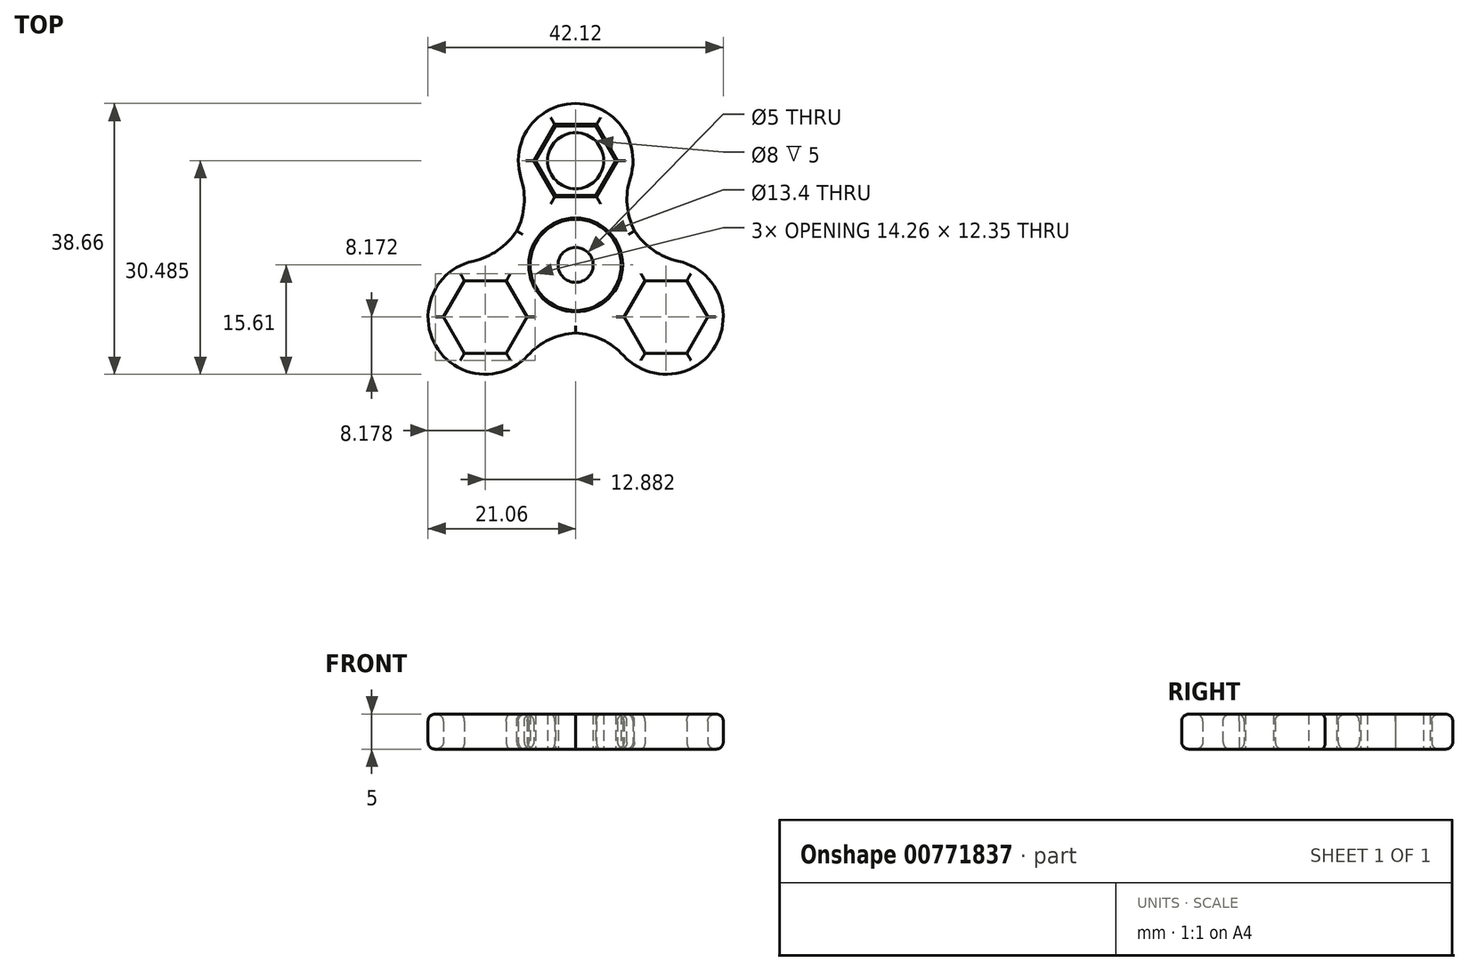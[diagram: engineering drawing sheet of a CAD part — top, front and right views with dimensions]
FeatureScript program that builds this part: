
annotation { "Feature Type Name" : "Feature", "Feature Type Description" : "" }
export const myFeature = defineFeature(function(context is Context, id is Id, definition is map)
    precondition{}
    {
        {
            assignVariable(context, id + "F0", {"name" : "Extrude", "anyValue" : 5});
        }
        {
            assignVariable(context, id + "F1", {"name" : "Brate", "anyValue" : 3});
        }
        {
            var Q0;
            Q0=qCreatedBy(makeId("Top.planeOp"),FACE);
            var sketch = newSketch(context, id + "F2", { "sketchPlane" : qUnion([Q0])});
            skCircle(sketch, "E0", {"center": v(0, 0) * mm, "radius": 2.5 * mm});
            skCircle(sketch, "E1", {"center": v(0, 0) * mm, "radius": 6.5 * mm});
            skCircle(sketch, "E2.0", {"center": v(0, 0) * mm, "radius": 6.7 * mm});
            skCircle(sketch, "E3.0", {"center": v(0, 0) * mm, "radius": 9.7 * mm});
            skCircle(sketch, "E4.cCircle", {"center": v(0, 14.88) * mm, "radius": 4.95 * mm, "construction": true});
            skLineSegment(sketch, "E4.0", {"start": v(5.72, 14.88) * mm, "end": v(2.86, 9.92) * mm});
            skLineSegment(sketch, "E4.1", {"start": v(2.86, 9.92) * mm, "end": v(-2.86, 9.92) * mm});
            skLineSegment(sketch, "E4.2", {"start": v(-2.86, 9.92) * mm, "end": v(-5.72, 14.88) * mm});
            skLineSegment(sketch, "E4.3", {"start": v(-5.72, 14.88) * mm, "end": v(-2.86, 19.83) * mm});
            skLineSegment(sketch, "E4.4", {"start": v(-2.86, 19.83) * mm, "end": v(2.86, 19.83) * mm});
            skLineSegment(sketch, "E4.5", {"start": v(2.86, 19.83) * mm, "end": v(5.72, 14.87) * mm});
            skPoint(sketch, "E4.0.midPoint", {"position": v(4.29, 12.4) * mm});
            skLineSegment(sketch, "E5.0", {"start": v(-2.99, 9.7) * mm, "end": v(-5.98, 14.88) * mm});
            skLineSegment(sketch, "E5.1", {"start": v(-2.99, 20.05) * mm, "end": v(2.99, 20.05) * mm});
            skLineSegment(sketch, "E5.2", {"start": v(2.99, 20.05) * mm, "end": v(5.98, 14.87) * mm});
            skLineSegment(sketch, "E5.3", {"start": v(-5.98, 14.88) * mm, "end": v(-2.99, 20.05) * mm});
            skLineSegment(sketch, "E5.4", {"start": v(5.98, 14.87) * mm, "end": v(2.99, 9.7) * mm});
            skLineSegment(sketch, "E5.5", {"start": v(2.99, 9.7) * mm, "end": v(-2.99, 9.7) * mm});
            skCircle(sketch, "E6.0", {"center": v(0, 14.88) * mm, "radius": 8.18 * mm});
            skCircle(sketch, "E7", {"center": v(0, 14.88) * mm, "radius": 4 * mm});
            skSolve(sketch);
        }
        {
            var Q0;
            {var subQ0=sQuery(id+"F2.wireOp",EDGE,"E5.0");Q0=makeQuery(id+"F2.imprint","IMPRINT",FACE,{"disambiguationData":[TD([[makeQuery(id+"F2.imprint","IMPRINT",EDGE,{"derivedFrom":subQ0}),1.0]])]});}
            var Q1;
            {var subQ0=sQuery(id+"F2.wireOp",EDGE,"E3.0");var subQ1=makeQuery(id+"F2.imprint","INTERSECT",VERTEX,{"derivedFrom":[subQ0,sQuery(id+"F2.wireOp",EDGE,"E5.5")]});Q1=makeQuery(id+"F2.imprint","IMPRINT",FACE,{"disambiguationData":[TD([[makeQuery(id+"F2.imprint","IMPRINT",EDGE,{"disambiguationData":[TD([[subQ1,1.0]])],"derivedFrom":subQ0}),1.0]])]});}
            var Q2;
            {var subQ0=sQuery(id+"F2.wireOp",EDGE,"E2.0");Q2=makeQuery(id+"F2.imprint","IMPRINT",FACE,{"disambiguationData":[TD([[makeQuery(id+"F2.imprint","IMPRINT",EDGE,{"derivedFrom":subQ0}),-1.0]])]});}
            extrude(context, id + "F3", {"entities" : qUnion([Q0, Q1, Q2]), "depth" : (getVariable(context, 'Extrude')) * mm, "offsetDistance" : 25 * mm});
        }
        {
            var Q0;
            {var subQ0=sQuery(id+"F2.wireOp",EDGE,"E3.0");var subQ1=sQuery(id+"F2.wireOp",EDGE,"1306070c-514a-42c6-8501-fb9c8bda2960.0");Q0=makeQuery(id+"F3.opExtrude","SWEPT_EDGE",EDGE,{"disambiguationData":[OSD([subQ1,subQ0]),TDD([makeQuery(id+"F2.imprint","INTERSECT",VERTEX,{"disambiguationData":[OD(0.0)],"derivedFrom":[subQ1,subQ0]})])]});}
            var Q1;
            {var subQ0=sQuery(id+"F2.wireOp",EDGE,"E3.0");var subQ1=sQuery(id+"F2.wireOp",EDGE,"1306070c-514a-42c6-8501-fb9c8bda2960.0");Q1=makeQuery(id+"F3.opExtrude","SWEPT_EDGE",EDGE,{"disambiguationData":[OSD([subQ1,subQ0]),TDD([makeQuery(id+"F2.imprint","INTERSECT",VERTEX,{"disambiguationData":[OD(1.0)],"derivedFrom":[subQ1,subQ0]})])]});}
            fillet(context, id + "F4", {"entities" : qUnion([Q0, Q1]), "radius" : 10 * mm, "tangentPropagation" : true, "allowEdgeOverflow" : false});
        }
        {
            var Q0;
            Q0=makeQuery(id+"F3.opExtrude","SWEPT_BODY",BODY,{"disambiguationData":[OSD([sQuery(id+"F2.wireOp",EDGE,"tQJWM1xx-dGoD-S2Vc-nebh-PP9qcAue4bdA"),sQuery(id+"F2.wireOp",EDGE,"a3c50200-fec0-4e6e-b60f-7094f83631b9.0"),sQuery(id+"F2.wireOp",EDGE,"6aacaa7e-477d-41c4-a672-bc6bc9144b92.0"),sQuery(id+"F2.wireOp",EDGE,"6aacaa7e-477d-41c4-a672-bc6bc9144b92.1"),sQuery(id+"F2.wireOp",EDGE,"6aacaa7e-477d-41c4-a672-bc6bc9144b92.2"),sQuery(id+"F2.wireOp",EDGE,"6aacaa7e-477d-41c4-a672-bc6bc9144b92.3"),sQuery(id+"F2.wireOp",EDGE,"6aacaa7e-477d-41c4-a672-bc6bc9144b92.4"),sQuery(id+"F2.wireOp",EDGE,"6aacaa7e-477d-41c4-a672-bc6bc9144b92.5"),sQuery(id+"F2.wireOp",EDGE,"f04c08d7-1c1c-44d0-9a47-92e5a5b5d3f8.1"),sQuery(id+"F2.wireOp",EDGE,"f04c08d7-1c1c-44d0-9a47-92e5a5b5d3f8.2"),sQuery(id+"F2.wireOp",EDGE,"f04c08d7-1c1c-44d0-9a47-92e5a5b5d3f8.3"),sQuery(id+"F2.wireOp",EDGE,"f04c08d7-1c1c-44d0-9a47-92e5a5b5d3f8.4"),sQuery(id+"F2.wireOp",EDGE,"UBTA8y4L-NzWo-JZS7-AoRI-JyAFkuAwjjts"),sQuery(id+"F2.wireOp",EDGE,"8978ab03-5a34-4537-871f-21df63c45cd8.0")])]});
            var Q1;
            Q1=makeQuery(id+"F3.opExtrude","SWEPT_BODY",BODY,{"disambiguationData":[OSD([sQuery(id+"F2.wireOp",EDGE,"bda56ee8-f399-41b0-afcc-1f5f46c89f62.0"),sQuery(id+"F2.wireOp",EDGE,"bda56ee8-f399-41b0-afcc-1f5f46c89f62.1"),sQuery(id+"F2.wireOp",EDGE,"bda56ee8-f399-41b0-afcc-1f5f46c89f62.2"),sQuery(id+"F2.wireOp",EDGE,"bda56ee8-f399-41b0-afcc-1f5f46c89f62.3"),sQuery(id+"F2.wireOp",EDGE,"bda56ee8-f399-41b0-afcc-1f5f46c89f62.4"),sQuery(id+"F2.wireOp",EDGE,"bda56ee8-f399-41b0-afcc-1f5f46c89f62.5"),sQuery(id+"F2.wireOp",EDGE,"1306070c-514a-42c6-8501-fb9c8bda2960.0"),sQuery(id+"F2.wireOp",EDGE,"E2.0"),sQuery(id+"F2.wireOp",EDGE,"E3.0")])]});
            var Q2;
            Q2=makeQuery(id+"F3.opExtrude","SWEPT_FACE",FACE,{"disambiguationData":[OSD([sQuery(id+"F2.wireOp",EDGE,"E3.0")])]});
            circularPattern(context, id + "F5", {"operationType" : NewBodyOperationType.ADD, "entities" : qUnion([Q0, Q1]), "axis" : qUnion([Q2]), "angle" : 360 * degree, "instanceCount" : getVariable(context, 'Brate'), "equalSpace" : true});
        }
        {
            var Q0;
            {var subQ0=makeQuery(id+"F3.opExtrude","CAP_FACE",FACE,{"disambiguationData":[OSD([sQuery(id+"F2.wireOp",EDGE,"E2.0"),sQuery(id+"F2.wireOp",EDGE,"E3.0"),sQuery(id+"F2.wireOp",EDGE,"E5.0"),sQuery(id+"F2.wireOp",EDGE,"E5.1"),sQuery(id+"F2.wireOp",EDGE,"E5.2"),sQuery(id+"F2.wireOp",EDGE,"E5.3"),sQuery(id+"F2.wireOp",EDGE,"E5.4"),sQuery(id+"F2.wireOp",EDGE,"E5.5"),sQuery(id+"F2.wireOp",EDGE,"E6.0")])],"isStart":false});Q0=makeQuery(id+"F5.boolean.opBoolean","MERGE",FACE,{"derivedFrom":[subQ0,makeQuery(id+"F5.opPattern","COPY",FACE,{"derivedFrom":subQ0,"instanceName":"1"}),makeQuery(id+"F5.opPattern","COPY",FACE,{"derivedFrom":subQ0,"instanceName":"2"})]});}
            var Q1;
            {var subQ0=makeQuery(id+"F3.opExtrude","CAP_FACE",FACE,{"disambiguationData":[OSD([sQuery(id+"F2.wireOp",EDGE,"E2.0"),sQuery(id+"F2.wireOp",EDGE,"E3.0"),sQuery(id+"F2.wireOp",EDGE,"E5.0"),sQuery(id+"F2.wireOp",EDGE,"E5.1"),sQuery(id+"F2.wireOp",EDGE,"E5.2"),sQuery(id+"F2.wireOp",EDGE,"E5.3"),sQuery(id+"F2.wireOp",EDGE,"E5.4"),sQuery(id+"F2.wireOp",EDGE,"E5.5"),sQuery(id+"F2.wireOp",EDGE,"E6.0")])],"isStart":true});Q1=makeQuery(id+"F5.boolean.opBoolean","MERGE",FACE,{"derivedFrom":[subQ0,makeQuery(id+"F5.opPattern","COPY",FACE,{"derivedFrom":subQ0,"instanceName":"1"}),makeQuery(id+"F5.opPattern","COPY",FACE,{"derivedFrom":subQ0,"instanceName":"2"})]});}
            fillet(context, id + "F6", {"entities" : qUnion([Q0, Q1]), "radius" : 1 * mm, "tangentPropagation" : true, "allowEdgeOverflow" : false});
        }
        {
            var Q0;
            Q0=makeQuery(id+"F2.imprint","IMPRINT",FACE,{"disambiguationData":[TD([[makeQuery(id+"F2.imprint","IMPRINT",EDGE,{"derivedFrom":sQuery(id+"F2.wireOp",EDGE,"E4.0")}),-1.0]])]});
            var Q1;
            Q1=makeQuery(id+"F2.imprint","IMPRINT",FACE,{"disambiguationData":[TD([[makeQuery(id+"F2.imprint","IMPRINT",EDGE,{"derivedFrom":sQuery(id+"F2.wireOp",EDGE,"E0")}),-1.0]])]});
            extrude(context, id + "F7", {"entities" : qUnion([Q0, Q1]), "depth" : 5 * mm, "offsetDistance" : 25 * mm});
        }
    });
